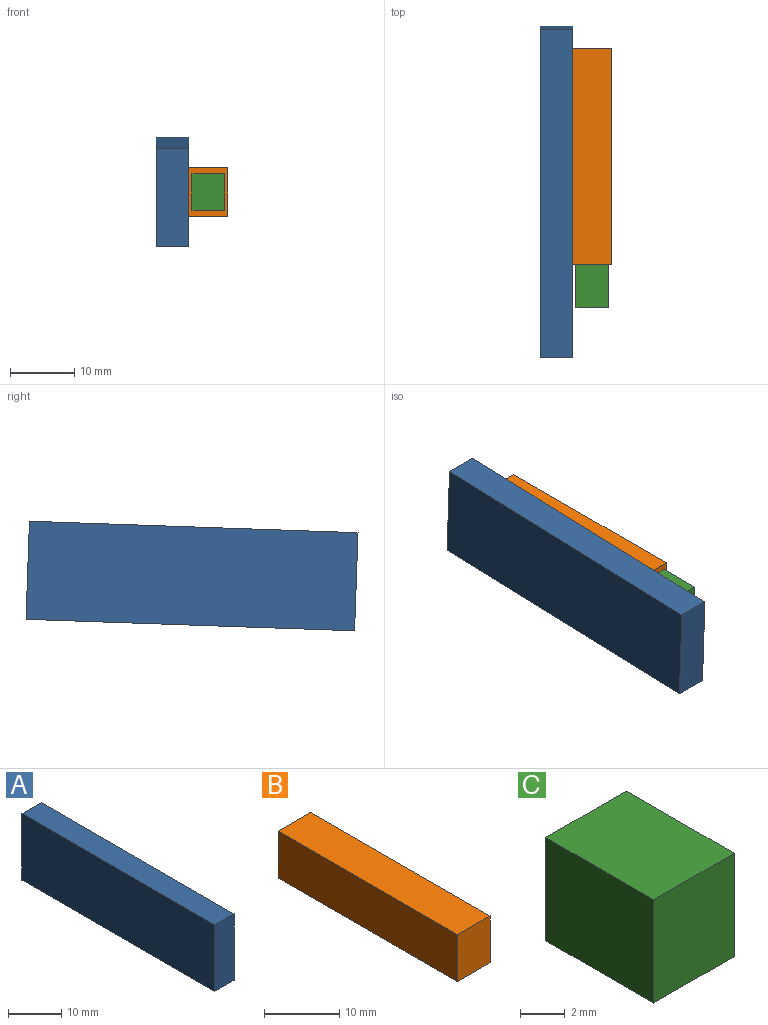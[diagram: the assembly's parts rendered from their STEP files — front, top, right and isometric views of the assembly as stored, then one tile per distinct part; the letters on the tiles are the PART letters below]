
ASSEMBLY  parts=3 mates=2
PART A: 6 faces, bbox 5.1x51.2x15.3 mm
  f0: plane 15.28x5.08mm, normal (0,-1,0), area 77.6mm2, adj f1,f3,f4,f5
  f1: plane 51.19x5.08mm, normal (0,0,-1), area 260mm2, adj f0,f2,f4,f5
  f2: plane 15.28x5.08mm, normal (0,1,0), area 77.6mm2, adj f1,f3,f4,f5
  f3: plane 51.19x5.08mm, normal (0,0,1), area 260mm2, adj f0,f2,f4,f5
  f4: plane 51.19x15.28mm, normal (1,0,0), area 782.3mm2, adj f0,f1,f2,f3
  f5: plane 51.19x15.28mm, normal (-1,0,0), area 782.3mm2, adj f0,f1,f2,f3
PART B: 6 faces, bbox 6.1x33.7x7.6 mm
  f0: plane 7.62x6.11mm, normal (0,1,0), area 46.6mm2, adj f1,f3,f4,f5
  f1: plane 33.66x7.62mm, normal (-1,0,0), area 256.5mm2, adj f0,f2,f4,f5
  f2: plane 7.62x6.11mm, normal (0,-1,0), area 46.6mm2, adj f1,f3,f4,f5
  f3: plane 33.66x7.62mm, normal (1,0,0), area 256.5mm2, adj f0,f2,f4,f5
  f4: plane 33.66x6.11mm, normal (0,0,1), area 205.7mm2, adj f0,f1,f2,f3
  f5: plane 33.66x6.11mm, normal (0,0,-1), area 205.7mm2, adj f0,f1,f2,f3
PART C: 6 faces, bbox 5.1x6.8x5.6 mm
  f0: plane 6.8x5.08mm, normal (0,0,1), area 34.6mm2, adj f1,f3,f4,f5
  f1: plane 5.64x5.08mm, normal (0,-1,0), area 28.6mm2, adj f0,f2,f4,f5
  f2: plane 6.8x5.08mm, normal (0,0,-1), area 34.6mm2, adj f1,f3,f4,f5
  f3: plane 5.64x5.08mm, normal (0,1,0), area 28.6mm2, adj f0,f2,f4,f5
  f4: plane 6.8x5.64mm, normal (1,0,0), area 38.3mm2, adj f0,f1,f2,f3
  f5: plane 6.8x5.64mm, normal (-1,0,0), area 38.3mm2, adj f0,f1,f2,f3
PLACE A rot(axis=(1,0,0),2deg) t=(3.87,-4.47,-0.03)mm
PLACE B t=(3.87,2.79,-0.2)mm
PLACE C t=(3.84,2.89,-0.02)mm
MATE pin_slot A.f4 <-> B.f1  axis (1,0,0) through (9.93,-16,3.61)mm
MATE fastened C.f3 <-> B.f2  axis (0,1,0) through (12.99,-27.24,3.61)mm
